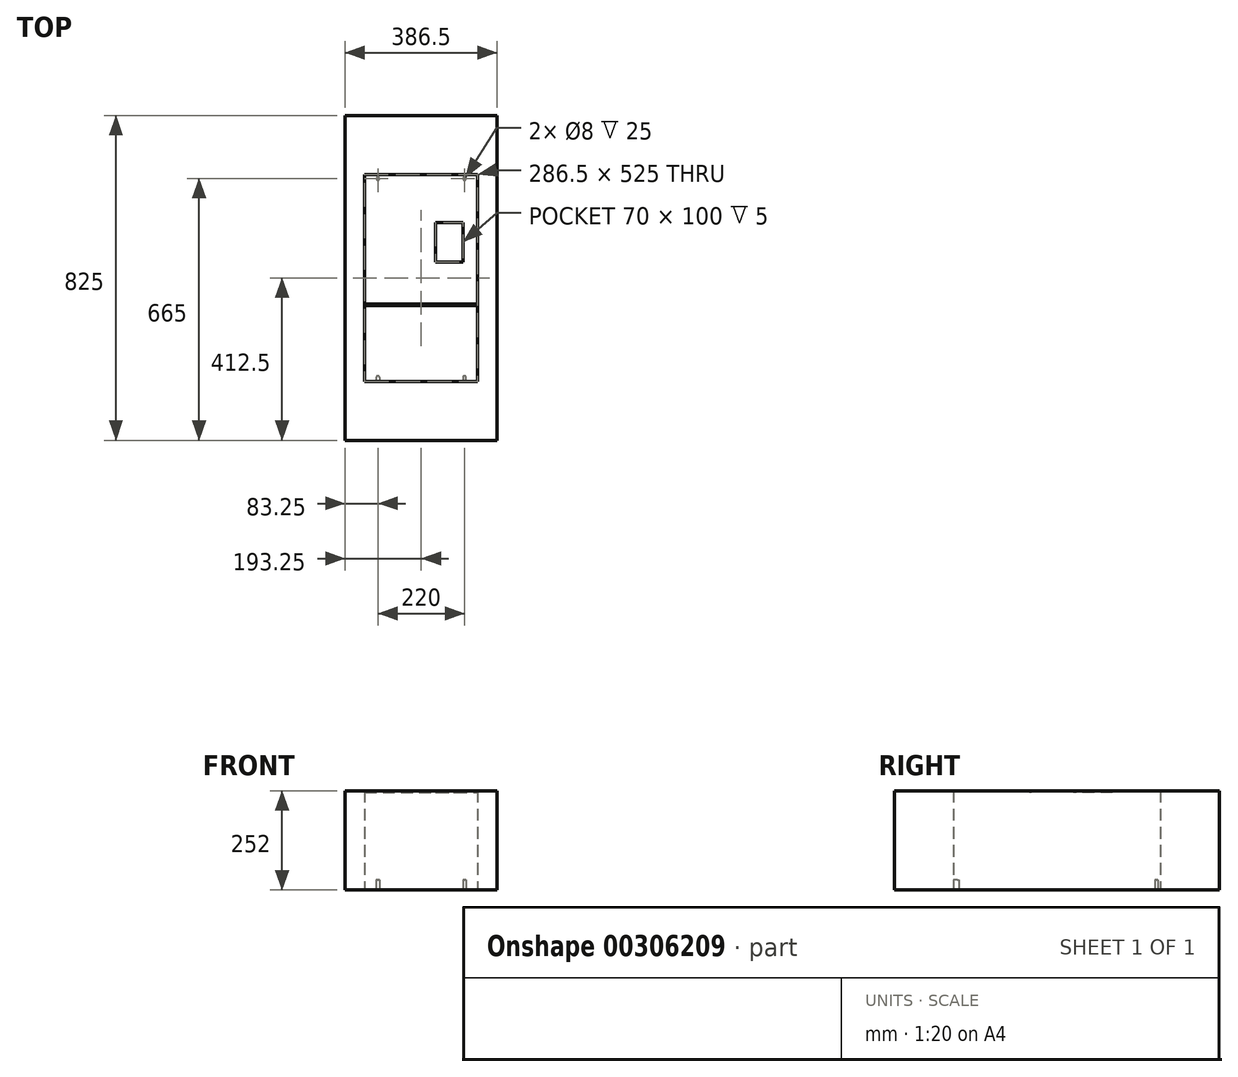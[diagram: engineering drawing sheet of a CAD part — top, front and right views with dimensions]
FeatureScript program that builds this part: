
annotation { "Feature Type Name" : "Feature", "Feature Type Description" : "" }
export const myFeature = defineFeature(function(context is Context, id is Id, definition is map)
    precondition{}
    {
        {
            var Q0;
            Q0=qCreatedBy(makeId("Top.planeOp"),FACE);
            var sketch = newSketch(context, id + "F0", { "sketchPlane" : qUnion([Q0])});
            skLineSegment(sketch, "E0.bottom", {"start": v(-143.25, 262.5) * mm, "end": v(143.25, 262.5) * mm});
            skLineSegment(sketch, "E0.top", {"start": v(-143.25, -262.5) * mm, "end": v(143.25, -262.5) * mm});
            skLineSegment(sketch, "E0.left", {"start": v(-143.25, 262.5) * mm, "end": v(-143.25, -262.5) * mm});
            skLineSegment(sketch, "E0.right", {"start": v(143.25, 262.5) * mm, "end": v(143.25, -262.5) * mm});
            skPoint(sketch, "E0.middle", {"position": v(0, 0) * mm});
            skCircle(sketch, "E1", {"center": v(-110, 252.5) * mm, "radius": 4 * mm});
            skCircle(sketch, "E2", {"center": v(110, 252.5) * mm, "radius": 4 * mm});
            skCircle(sketch, "E3", {"center": v(-110, -252.5) * mm, "radius": 4 * mm});
            skCircle(sketch, "E4", {"center": v(110, -252.5) * mm, "radius": 4 * mm});
            skLineSegment(sketch, "E5", {"start": v(-114, -252.5) * mm, "end": v(-114, -262.5) * mm});
            skLineSegment(sketch, "E6", {"start": v(-106, -252.5) * mm, "end": v(-106, -262.5) * mm});
            skLineSegment(sketch, "E7", {"start": v(114, -262.5) * mm, "end": v(114, -252.5) * mm});
            skLineSegment(sketch, "E8", {"start": v(106, -252.5) * mm, "end": v(106, -262.5) * mm});
            skLineSegment(sketch, "E9", {"start": v(0, -262.5) * mm, "end": v(0, 262.5) * mm, "construction": true});
            skLineSegment(sketch, "E10", {"start": v(-143.25, 0) * mm, "end": v(143.25, 0) * mm, "construction": true});
            skSolve(sketch);
        }
        {
            var Q0;
            Q0=makeQuery(id+"F0.imprint","IMPRINT",FACE,{"disambiguationData":[TD([[makeQuery(id+"F0.imprint","IMPRINT",EDGE,{"derivedFrom":sQuery(id+"F0.wireOp",EDGE,"E0.bottom")}),-1.0]])]});
            var Q1;
            {var subQ0=sQuery(id+"F0.wireOp",EDGE,"E6");var subQ1=sQuery(id+"F0.wireOp",EDGE,"E3");var subQ2=makeQuery(id+"F0.imprint","INTERSECT",VERTEX,{"disambiguationData":[OD(0.0)],"derivedFrom":[subQ1,subQ0]});Q1=makeQuery(id+"F0.imprint","IMPRINT",FACE,{"disambiguationData":[TD([[makeQuery(id+"F0.imprint","IMPRINT",EDGE,{"disambiguationData":[TD([[subQ2,1.0]])],"derivedFrom":subQ1}),1.0]])]});}
            var Q2;
            {var subQ0=sQuery(id+"F0.wireOp",EDGE,"E5");Q2=makeQuery(id+"F0.imprint","IMPRINT",FACE,{"disambiguationData":[TD([[makeQuery(id+"F0.imprint","IMPRINT",EDGE,{"derivedFrom":subQ0}),1.0]])]});}
            var Q3;
            {var subQ0=sQuery(id+"F0.wireOp",EDGE,"E4");var subQ1=makeQuery(id+"F0.imprint","INTERSECT",VERTEX,{"derivedFrom":[subQ0,sQuery(id+"F0.wireOp",EDGE,"E7")]});Q3=makeQuery(id+"F0.imprint","IMPRINT",FACE,{"disambiguationData":[TD([[makeQuery(id+"F0.imprint","IMPRINT",EDGE,{"disambiguationData":[TD([[subQ1,1.0]])],"derivedFrom":subQ0}),1.0]])]});}
            var Q4;
            {var subQ0=sQuery(id+"F0.wireOp",EDGE,"E7");Q4=makeQuery(id+"F0.imprint","IMPRINT",FACE,{"disambiguationData":[TD([[makeQuery(id+"F0.imprint","IMPRINT",EDGE,{"derivedFrom":subQ0}),1.0]])]});}
            var Q5;
            Q5=makeQuery(id+"F0.imprint","IMPRINT",FACE,{"disambiguationData":[TD([[makeQuery(id+"F0.imprint","IMPRINT",EDGE,{"derivedFrom":sQuery(id+"F0.wireOp",EDGE,"E1")}),1.0]])]});
            var Q6;
            Q6=makeQuery(id+"F0.imprint","IMPRINT",FACE,{"disambiguationData":[TD([[makeQuery(id+"F0.imprint","IMPRINT",EDGE,{"derivedFrom":sQuery(id+"F0.wireOp",EDGE,"E2")}),1.0]])]});
            extrude(context, id + "F1", {"entities" : qUnion([Q0, Q1, Q2, Q3, Q4, Q5, Q6]), "depth" : 252 * mm});
        }
        {
            var Q0;
            {var subQ0=sQuery(id+"F0.wireOp",EDGE,"E6");var subQ1=sQuery(id+"F0.wireOp",EDGE,"E3");var subQ2=makeQuery(id+"F0.imprint","INTERSECT",VERTEX,{"disambiguationData":[OD(0.0)],"derivedFrom":[subQ1,subQ0]});Q0=makeQuery(id+"F0.imprint","IMPRINT",FACE,{"disambiguationData":[TD([[makeQuery(id+"F0.imprint","IMPRINT",EDGE,{"disambiguationData":[TD([[subQ2,1.0]])],"derivedFrom":subQ1}),1.0]])]});}
            var Q1;
            {var subQ0=sQuery(id+"F0.wireOp",EDGE,"E5");Q1=makeQuery(id+"F0.imprint","IMPRINT",FACE,{"disambiguationData":[TD([[makeQuery(id+"F0.imprint","IMPRINT",EDGE,{"derivedFrom":subQ0}),1.0]])]});}
            var Q2;
            {var subQ0=sQuery(id+"F0.wireOp",EDGE,"E7");Q2=makeQuery(id+"F0.imprint","IMPRINT",FACE,{"disambiguationData":[TD([[makeQuery(id+"F0.imprint","IMPRINT",EDGE,{"derivedFrom":subQ0}),1.0]])]});}
            var Q3;
            {var subQ0=sQuery(id+"F0.wireOp",EDGE,"E4");var subQ1=makeQuery(id+"F0.imprint","INTERSECT",VERTEX,{"derivedFrom":[subQ0,sQuery(id+"F0.wireOp",EDGE,"E7")]});Q3=makeQuery(id+"F0.imprint","IMPRINT",FACE,{"disambiguationData":[TD([[makeQuery(id+"F0.imprint","IMPRINT",EDGE,{"disambiguationData":[TD([[subQ1,1.0]])],"derivedFrom":subQ0}),1.0]])]});}
            var Q4;
            Q4=makeQuery(id+"F0.imprint","IMPRINT",FACE,{"disambiguationData":[TD([[makeQuery(id+"F0.imprint","IMPRINT",EDGE,{"derivedFrom":sQuery(id+"F0.wireOp",EDGE,"E2")}),1.0]])]});
            var Q5;
            Q5=makeQuery(id+"F0.imprint","IMPRINT",FACE,{"disambiguationData":[TD([[makeQuery(id+"F0.imprint","IMPRINT",EDGE,{"derivedFrom":sQuery(id+"F0.wireOp",EDGE,"E1")}),1.0]])]});
            extrude(context, id + "F2", {"entities" : qUnion([Q0, Q1, Q2, Q3, Q4, Q5]), "operationType" : NewBodyOperationType.REMOVE, "depth" : 25 * mm});
        }
        {
            var Q0;
            Q0=makeQuery(id+"F1.opExtrude","CAP_FACE",FACE,{"disambiguationData":[OSD([sQuery(id+"F0.wireOp",EDGE,"E0.bottom"),sQuery(id+"F0.wireOp",EDGE,"E0.top"),sQuery(id+"F0.wireOp",EDGE,"E0.left"),sQuery(id+"F0.wireOp",EDGE,"E0.right"),sQuery(id+"F0.wireOp",EDGE,"E3"),sQuery(id+"F0.wireOp",EDGE,"E6")])],"isStart":false});
            var sketch = newSketch(context, id + "F3", { "sketchPlane" : qUnion([Q0])});
            skLineSegment(sketch, "E11.bottom", {"start": v(36.31, 141.06) * mm, "end": v(106.31, 141.06) * mm});
            skLineSegment(sketch, "E11.top", {"start": v(36.31, 41.06) * mm, "end": v(106.31, 41.06) * mm});
            skLineSegment(sketch, "E11.left", {"start": v(36.31, 141.06) * mm, "end": v(36.31, 41.06) * mm});
            skLineSegment(sketch, "E11.right", {"start": v(106.31, 141.06) * mm, "end": v(106.31, 41.06) * mm});
            skPoint(sketch, "E11.middle", {"position": v(71.31, 91.06) * mm});
            skLineSegment(sketch, "E12", {"start": v(-143.25, -65.55) * mm, "end": v(143.25, -65.55) * mm});
            skLineSegment(sketch, "E13", {"start": v(143.25, -65.55) * mm, "end": v(143.25, -70.55) * mm});
            skLineSegment(sketch, "E14", {"start": v(143.25, -70.55) * mm, "end": v(-143.25, -70.55) * mm});
            skSolve(sketch);
        }
        {
            var Q0;
            Q0=makeQuery(id+"F3.imprint","IMPRINT",FACE,{"disambiguationData":[TD([[makeQuery(id+"F3.imprint","IMPRINT",EDGE,{"derivedFrom":sQuery(id+"F3.wireOp",EDGE,"E11.bottom")}),-1.0]])]});
            var Q1;
            {var subQ0=sQuery(id+"F3.wireOp",EDGE,"E12");Q1=makeQuery(id+"F3.imprint","IMPRINT",FACE,{"disambiguationData":[TD([[makeQuery(id+"F3.imprint","IMPRINT",EDGE,{"derivedFrom":subQ0}),-1.0]])]});}
            extrude(context, id + "F4", {"entities" : qUnion([Q0, Q1]), "operationType" : NewBodyOperationType.REMOVE, "oppositeDirection" : true, "depth" : 5 * mm});
        }
        {
            var Q0;
            Q0=makeQuery(id+"F1.opExtrude","CAP_FACE",FACE,{"disambiguationData":[OSD([sQuery(id+"F0.wireOp",EDGE,"E0.bottom"),sQuery(id+"F0.wireOp",EDGE,"E0.top"),sQuery(id+"F0.wireOp",EDGE,"E0.left"),sQuery(id+"F0.wireOp",EDGE,"E0.right"),sQuery(id+"F0.wireOp",EDGE,"E3"),sQuery(id+"F0.wireOp",EDGE,"E6")])],"isStart":true});
            var sketch = newSketch(context, id + "F5", { "sketchPlane" : qUnion([Q0])});
            skLineSegment(sketch, "E15.0", {"start": v(-143.25, -262.5) * mm, "end": v(-143.25, 262.5) * mm});
            skLineSegment(sketch, "E15.1", {"start": v(143.25, -262.5) * mm, "end": v(143.25, 262.5) * mm});
            skLineSegment(sketch, "E15.2", {"start": v(-143.25, -262.5) * mm, "end": v(143.25, -262.5) * mm});
            skLineSegment(sketch, "E16", {"start": v(-143.25, 262.5) * mm, "end": v(143.25, 262.5) * mm});
            skLineSegment(sketch, "E17.bottom", {"start": v(143.25, 262.5) * mm, "end": v(193.25, 262.5) * mm, "construction": true});
            skLineSegment(sketch, "E17.right", {"start": v(193.25, 262.5) * mm, "end": v(193.25, -262.5) * mm});
            skLineSegment(sketch, "E18.bottom", {"start": v(-143.25, 262.5) * mm, "end": v(-193.25, 262.5) * mm, "construction": true});
            skLineSegment(sketch, "E18.top", {"start": v(-143.25, -262.5) * mm, "end": v(-193.25, -262.5) * mm, "construction": true});
            skLineSegment(sketch, "E18.left", {"start": v(-143.25, 262.5) * mm, "end": v(-143.25, -262.5) * mm});
            skLineSegment(sketch, "E18.right", {"start": v(-193.25, 262.5) * mm, "end": v(-193.25, -262.5) * mm});
            skLineSegment(sketch, "E19.top", {"start": v(-193.25, 412.5) * mm, "end": v(193.25, 412.5) * mm});
            skLineSegment(sketch, "E19.left", {"start": v(-193.25, 262.5) * mm, "end": v(-193.25, 412.5) * mm});
            skLineSegment(sketch, "E19.right", {"start": v(193.25, 262.5) * mm, "end": v(193.25, 412.5) * mm});
            skLineSegment(sketch, "E20.top", {"start": v(-193.25, -412.5) * mm, "end": v(193.25, -412.5) * mm});
            skLineSegment(sketch, "E20.left", {"start": v(-193.25, -262.5) * mm, "end": v(-193.25, -412.5) * mm});
            skLineSegment(sketch, "E20.right", {"start": v(193.25, -262.5) * mm, "end": v(193.25, -412.5) * mm});
            skLineSegment(sketch, "E21", {"start": v(143.25, -262.5) * mm, "end": v(193.25, -262.5) * mm, "construction": true});
            skSolve(sketch);
        }
        {
            var Q0;
            {var subQ2=sQuery(id+"F5.wireOp",EDGE,"E15.1");Q0=makeQuery(id+"F5.imprint","IMPRINT",FACE,{"disambiguationData":[TD([[makeQuery(id+"F5.imprint","IMPRINT",EDGE,{"derivedFrom":subQ2}),-1.0]])]});}
            extrude(context, id + "F6", {"entities" : qUnion([Q0]), "oppositeDirection" : true, "depth" : 252 * mm});
        }
    });
